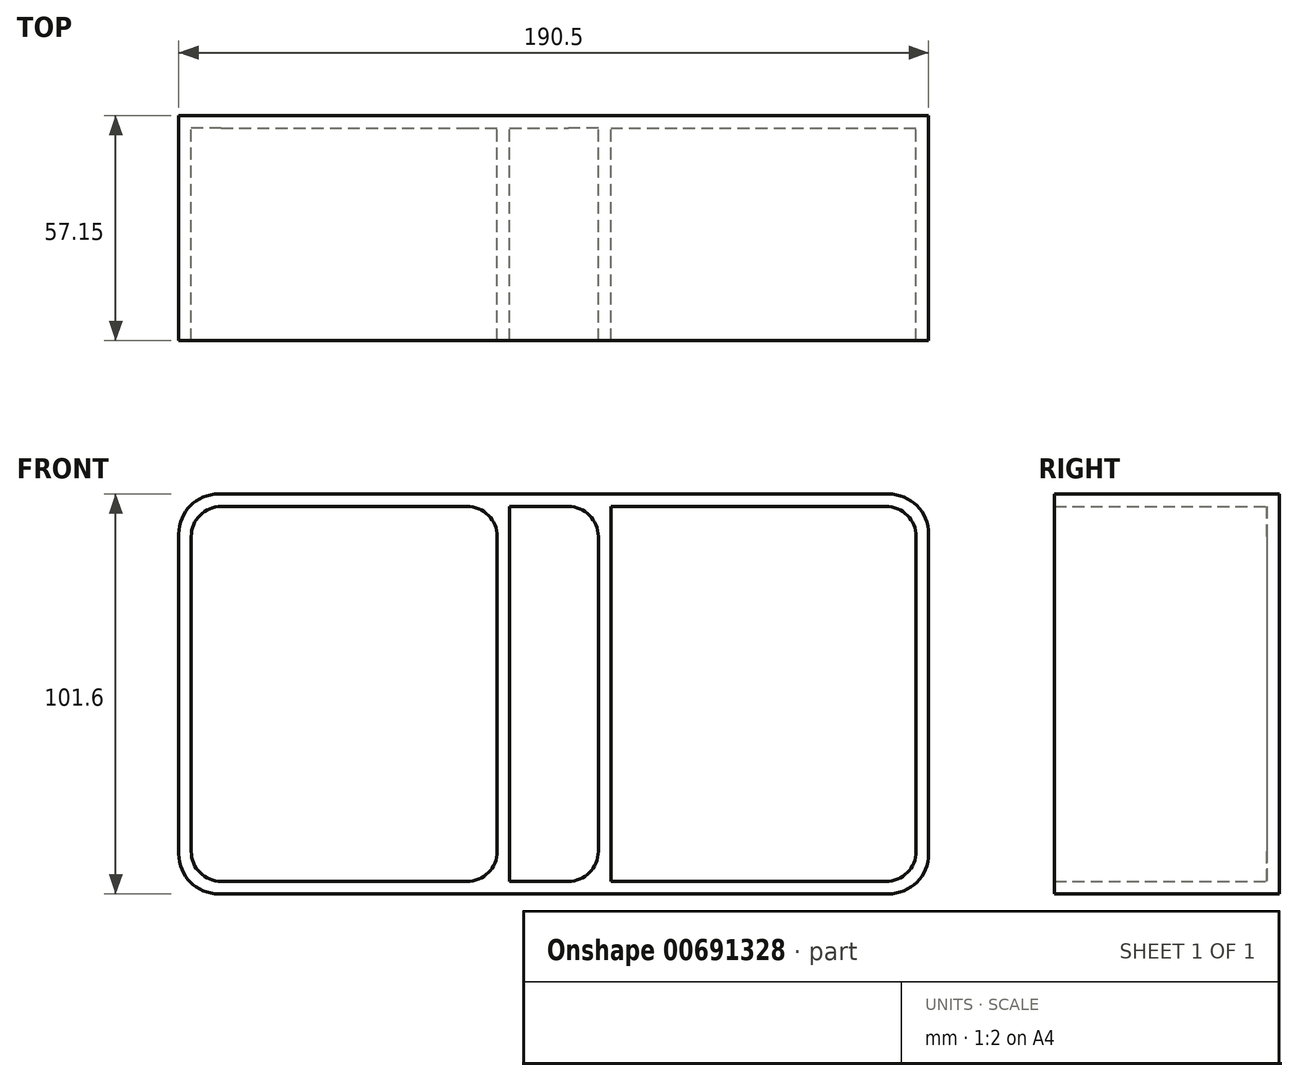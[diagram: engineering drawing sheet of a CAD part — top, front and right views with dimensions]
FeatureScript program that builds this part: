
annotation { "Feature Type Name" : "Feature", "Feature Type Description" : "" }
export const myFeature = defineFeature(function(context is Context, id is Id, definition is map)
    precondition{}
    {
        {
            var Q0;
            Q0=qCreatedBy(makeId("Front.planeOp"),FACE);
            var sketch = newSketch(context, id + "F0", { "sketchPlane" : qUnion([Q0])});
            skLineSegment(sketch, "E0.bottom", {"start": v(-81.88, 40.07) * mm, "end": v(108.62, 40.07) * mm});
            skLineSegment(sketch, "E0.top", {"start": v(-81.88, -61.53) * mm, "end": v(108.62, -61.53) * mm});
            skLineSegment(sketch, "E0.left", {"start": v(-81.88, 40.07) * mm, "end": v(-81.88, -61.53) * mm});
            skLineSegment(sketch, "E0.right", {"start": v(108.62, 40.07) * mm, "end": v(108.62, -61.53) * mm});
            skSolve(sketch);
        }
        {
            var Q0;
            Q0 = qSketchRegion(id + "F0", true);
            extrude(context, id + "F1", {"entities" : qUnion([Q0]), "depth" : 3.17 * mm, "offsetDistance" : 25.4 * mm});
        }
        {
            var Q0;
            Q0=makeQuery(id+"F1.opExtrude","CAP_FACE",FACE,{"disambiguationData":[OSD([sQuery(id+"F0.wireOp",EDGE,"E0.bottom"),sQuery(id+"F0.wireOp",EDGE,"E0.top"),sQuery(id+"F0.wireOp",EDGE,"E0.left"),sQuery(id+"F0.wireOp",EDGE,"E0.right")])],"isStart":false});
            var sketch = newSketch(context, id + "F2", { "sketchPlane" : qUnion([Q0])});
            skLineSegment(sketch, "E1.bottom", {"start": v(108.62, 40.07) * mm, "end": v(105.44, 40.07) * mm});
            skLineSegment(sketch, "E1.top", {"start": v(108.62, -61.53) * mm, "end": v(105.44, -61.53) * mm});
            skLineSegment(sketch, "E1.left", {"start": v(108.62, 40.07) * mm, "end": v(108.62, -61.53) * mm});
            skLineSegment(sketch, "E1.right", {"start": v(105.44, 40.07) * mm, "end": v(105.44, -61.53) * mm});
            skLineSegment(sketch, "E2.bottom", {"start": v(-81.88, 40.07) * mm, "end": v(-78.7, 40.07) * mm});
            skLineSegment(sketch, "E2.top", {"start": v(-81.88, -61.53) * mm, "end": v(-78.7, -61.53) * mm});
            skLineSegment(sketch, "E2.left", {"start": v(-81.88, 40.07) * mm, "end": v(-81.88, -61.53) * mm});
            skLineSegment(sketch, "E2.right", {"start": v(-78.7, 40.07) * mm, "end": v(-78.7, -61.53) * mm});
            skLineSegment(sketch, "E3.bottom", {"start": v(-78.7, 40.07) * mm, "end": v(105.44, 40.07) * mm});
            skLineSegment(sketch, "E3.top", {"start": v(-78.7, 36.9) * mm, "end": v(105.44, 36.9) * mm});
            skLineSegment(sketch, "E3.left", {"start": v(-78.7, 40.07) * mm, "end": v(-78.7, 36.9) * mm});
            skLineSegment(sketch, "E3.right", {"start": v(105.44, 40.07) * mm, "end": v(105.44, 36.9) * mm});
            skLineSegment(sketch, "E4.bottom", {"start": v(-78.7, -61.53) * mm, "end": v(105.44, -61.53) * mm});
            skLineSegment(sketch, "E4.top", {"start": v(-78.7, -58.36) * mm, "end": v(105.44, -58.36) * mm});
            skLineSegment(sketch, "E4.left", {"start": v(-78.7, -61.53) * mm, "end": v(-78.7, -58.36) * mm});
            skLineSegment(sketch, "E4.right", {"start": v(105.44, -61.53) * mm, "end": v(105.44, -58.36) * mm});
            skSolve(sketch);
        }
        {
            var Q0;
            Q0 = qSketchRegion(id + "F2", true);
            extrude(context, id + "F3", {"entities" : qUnion([Q0]), "operationType" : NewBodyOperationType.ADD, "depth" : 53.97 * mm, "offsetDistance" : 25.4 * mm});
        }
        {
            var Q0;
            Q0=makeQuery(id+"F1.opExtrude","CAP_FACE",FACE,{"disambiguationData":[OSD([sQuery(id+"F0.wireOp",EDGE,"E0.bottom"),sQuery(id+"F0.wireOp",EDGE,"E0.top"),sQuery(id+"F0.wireOp",EDGE,"E0.left"),sQuery(id+"F0.wireOp",EDGE,"E0.right")])],"isStart":false});
            var sketch = newSketch(context, id + "F4", { "sketchPlane" : qUnion([Q0])});
            skLineSegment(sketch, "E5.bottom", {"start": v(-0.98, 36.9) * mm, "end": v(2.2, 36.9) * mm});
            skLineSegment(sketch, "E5.top", {"start": v(-0.98, -58.36) * mm, "end": v(2.2, -58.36) * mm});
            skLineSegment(sketch, "E5.left", {"start": v(-0.98, 36.9) * mm, "end": v(-0.98, -58.36) * mm});
            skLineSegment(sketch, "E5.right", {"start": v(2.2, 36.9) * mm, "end": v(2.2, -58.36) * mm});
            skSolve(sketch);
        }
        {
            var Q0;
            Q0 = qSketchRegion(id + "F4", true);
            extrude(context, id + "F5", {"entities" : qUnion([Q0]), "operationType" : NewBodyOperationType.ADD, "depth" : 53.97 * mm, "offsetDistance" : 25.4 * mm});
        }
        {
            var Q0;
            Q0=makeQuery(id+"F5.opExtrude","SWEPT_EDGE",EDGE,{"disambiguationData":[OSD([sQuery(id+"F2.wireOp",EDGE,"E4.top"),sQuery(id+"F4.wireOp",EDGE,"E5.top"),sQuery(id+"F4.wireOp",EDGE,"E5.left")])]});
            var Q1;
            Q1=makeQuery(id+"F5.opExtrude","SWEPT_EDGE",EDGE,{"disambiguationData":[OSD([sQuery(id+"F2.wireOp",EDGE,"E3.top"),sQuery(id+"F4.wireOp",EDGE,"E5.bottom"),sQuery(id+"F4.wireOp",EDGE,"E5.right")])]});
            var Q2;
            Q2=makeQuery(id+"F5.opExtrude","SWEPT_EDGE",EDGE,{"disambiguationData":[OSD([sQuery(id+"F2.wireOp",EDGE,"E4.top"),sQuery(id+"F4.wireOp",EDGE,"E5.top"),sQuery(id+"F4.wireOp",EDGE,"E5.right")])]});
            var Q3;
            Q3=makeQuery(id+"F5.opExtrude","SWEPT_EDGE",EDGE,{"disambiguationData":[OSD([sQuery(id+"F2.wireOp",EDGE,"E3.top"),sQuery(id+"F4.wireOp",EDGE,"E5.bottom"),sQuery(id+"F4.wireOp",EDGE,"E5.left")])]});
            fillet(context, id + "F6", {"entities" : qUnion([Q0, Q1, Q2, Q3]), "radius" : 7.62 * mm, "tangentPropagation" : true, "allowEdgeOverflow" : false});
        }
        {
            var Q0;
            Q0=makeQuery(id+"F3.opExtrude","SWEPT_EDGE",EDGE,{"disambiguationData":[OSD([sQuery(id+"F2.wireOp",EDGE,"E2.right"),sQuery(id+"F2.wireOp",EDGE,"E4.top"),sQuery(id+"F2.wireOp",EDGE,"E4.left")])]});
            var Q1;
            Q1=makeQuery(id+"F3.opExtrude","SWEPT_EDGE",EDGE,{"disambiguationData":[OSD([sQuery(id+"F2.wireOp",EDGE,"E2.right"),sQuery(id+"F2.wireOp",EDGE,"E3.top"),sQuery(id+"F2.wireOp",EDGE,"E3.left")])]});
            fillet(context, id + "F7", {"entities" : qUnion([Q0, Q1]), "radius" : 7.62 * mm, "tangentPropagation" : true, "allowEdgeOverflow" : false});
        }
        {
            var Q0;
            Q0=makeQuery(id+"F5.boolean.opBoolean","SPLIT",FACE,{"disambiguationData":[TD([makeQuery(id+"F3.opExtrude","SWEPT_FACE",FACE,{"disambiguationData":[OSD([sQuery(id+"F2.wireOp",EDGE,"E1.right")])]})])],"derivedFrom":makeQuery(id+"F1.opExtrude","CAP_FACE",FACE,{"disambiguationData":[OSD([sQuery(id+"F0.wireOp",EDGE,"E0.bottom"),sQuery(id+"F0.wireOp",EDGE,"E0.top"),sQuery(id+"F0.wireOp",EDGE,"E0.left"),sQuery(id+"F0.wireOp",EDGE,"E0.right")])],"isStart":false})});
            var sketch = newSketch(context, id + "F8", { "sketchPlane" : qUnion([Q0])});
            skLineSegment(sketch, "E6.bottom", {"start": v(27.88, 36.9) * mm, "end": v(24.7, 36.9) * mm});
            skLineSegment(sketch, "E6.top", {"start": v(27.88, -58.36) * mm, "end": v(24.7, -58.36) * mm});
            skLineSegment(sketch, "E6.left", {"start": v(27.88, 36.9) * mm, "end": v(27.88, -58.36) * mm});
            skLineSegment(sketch, "E6.right", {"start": v(24.7, 36.9) * mm, "end": v(24.7, -58.36) * mm});
            skSolve(sketch);
        }
        {
            var Q0;
            Q0 = qSketchRegion(id + "F8", true);
            extrude(context, id + "F9", {"entities" : qUnion([Q0]), "operationType" : NewBodyOperationType.ADD, "depth" : 53.97 * mm, "offsetDistance" : 25.4 * mm});
        }
        {
            var Q0;
            Q0=makeQuery(id+"F9.opExtrude","SWEPT_EDGE",EDGE,{"disambiguationData":[OSD([sQuery(id+"F2.wireOp",EDGE,"E4.top"),sQuery(id+"F8.wireOp",EDGE,"E6.top"),sQuery(id+"F8.wireOp",EDGE,"E6.right")])]});
            var Q1;
            Q1=makeQuery(id+"F9.opExtrude","SWEPT_EDGE",EDGE,{"disambiguationData":[OSD([sQuery(id+"F2.wireOp",EDGE,"E3.top"),sQuery(id+"F8.wireOp",EDGE,"E6.bottom"),sQuery(id+"F8.wireOp",EDGE,"E6.right")])]});
            var Q2;
            Q2=makeQuery(id+"F9.opExtrude","SWEPT_EDGE",EDGE,{"disambiguationData":[OSD([sQuery(id+"F2.wireOp",EDGE,"E3.top"),sQuery(id+"F8.wireOp",EDGE,"E6.bottom"),sQuery(id+"F8.wireOp",EDGE,"E6.left")])]});
            var Q3;
            Q3=makeQuery(id+"F9.opExtrude","SWEPT_EDGE",EDGE,{"disambiguationData":[OSD([sQuery(id+"F2.wireOp",EDGE,"E4.top"),sQuery(id+"F8.wireOp",EDGE,"E6.top"),sQuery(id+"F8.wireOp",EDGE,"E6.left")])]});
            fillet(context, id + "F10", {"entities" : qUnion([Q0, Q1, Q2, Q3]), "radius" : 7.62 * mm, "tangentPropagation" : true, "allowEdgeOverflow" : false});
        }
        {
            var Q0;
            Q0=makeQuery(id+"F3.opExtrude","SWEPT_EDGE",EDGE,{"disambiguationData":[OSD([sQuery(id+"F2.wireOp",EDGE,"E1.right"),sQuery(id+"F2.wireOp",EDGE,"E3.top"),sQuery(id+"F2.wireOp",EDGE,"E3.right")])]});
            var Q1;
            Q1=makeQuery(id+"F3.opExtrude","SWEPT_EDGE",EDGE,{"disambiguationData":[OSD([sQuery(id+"F2.wireOp",EDGE,"E1.right"),sQuery(id+"F2.wireOp",EDGE,"E4.top"),sQuery(id+"F2.wireOp",EDGE,"E4.right")])]});
            fillet(context, id + "F11", {"entities" : qUnion([Q0, Q1]), "radius" : 7.62 * mm, "tangentPropagation" : true, "allowEdgeOverflow" : false});
        }
        {
            var Q0;
            Q0=makeQuery(id+"F3.boolean.opBoolean","MERGE",EDGE,{"derivedFrom":[makeQuery(id+"F1.opExtrude","SWEPT_EDGE",EDGE,{"disambiguationData":[OSD([sQuery(id+"F0.wireOp",EDGE,"E0.top"),sQuery(id+"F0.wireOp",EDGE,"E0.left")])]}),makeQuery(id+"F3.opExtrude","SWEPT_EDGE",EDGE,{"disambiguationData":[OSD([sQuery(id+"F2.wireOp",EDGE,"E2.top"),sQuery(id+"F2.wireOp",EDGE,"E2.left")])]})]});
            var Q1;
            Q1=makeQuery(id+"F3.boolean.opBoolean","MERGE",EDGE,{"derivedFrom":[makeQuery(id+"F1.opExtrude","SWEPT_EDGE",EDGE,{"disambiguationData":[OSD([sQuery(id+"F0.wireOp",EDGE,"E0.top"),sQuery(id+"F0.wireOp",EDGE,"E0.right")])]}),makeQuery(id+"F3.opExtrude","SWEPT_EDGE",EDGE,{"disambiguationData":[OSD([sQuery(id+"F2.wireOp",EDGE,"E1.top"),sQuery(id+"F2.wireOp",EDGE,"E1.left")])]})]});
            var Q2;
            Q2=makeQuery(id+"F3.boolean.opBoolean","MERGE",EDGE,{"derivedFrom":[makeQuery(id+"F1.opExtrude","SWEPT_EDGE",EDGE,{"disambiguationData":[OSD([sQuery(id+"F0.wireOp",EDGE,"E0.bottom"),sQuery(id+"F0.wireOp",EDGE,"E0.right")])]}),makeQuery(id+"F3.opExtrude","SWEPT_EDGE",EDGE,{"disambiguationData":[OSD([sQuery(id+"F2.wireOp",EDGE,"E1.bottom"),sQuery(id+"F2.wireOp",EDGE,"E1.left")])]})]});
            var Q3;
            Q3=makeQuery(id+"F3.boolean.opBoolean","MERGE",EDGE,{"derivedFrom":[makeQuery(id+"F1.opExtrude","SWEPT_EDGE",EDGE,{"disambiguationData":[OSD([sQuery(id+"F0.wireOp",EDGE,"E0.bottom"),sQuery(id+"F0.wireOp",EDGE,"E0.left")])]}),makeQuery(id+"F3.opExtrude","SWEPT_EDGE",EDGE,{"disambiguationData":[OSD([sQuery(id+"F2.wireOp",EDGE,"E2.bottom"),sQuery(id+"F2.wireOp",EDGE,"E2.left")])]})]});
            fillet(context, id + "F12", {"entities" : qUnion([Q0, Q1, Q2, Q3]), "radius" : 10.16 * mm, "tangentPropagation" : true, "allowEdgeOverflow" : false});
        }
    });
